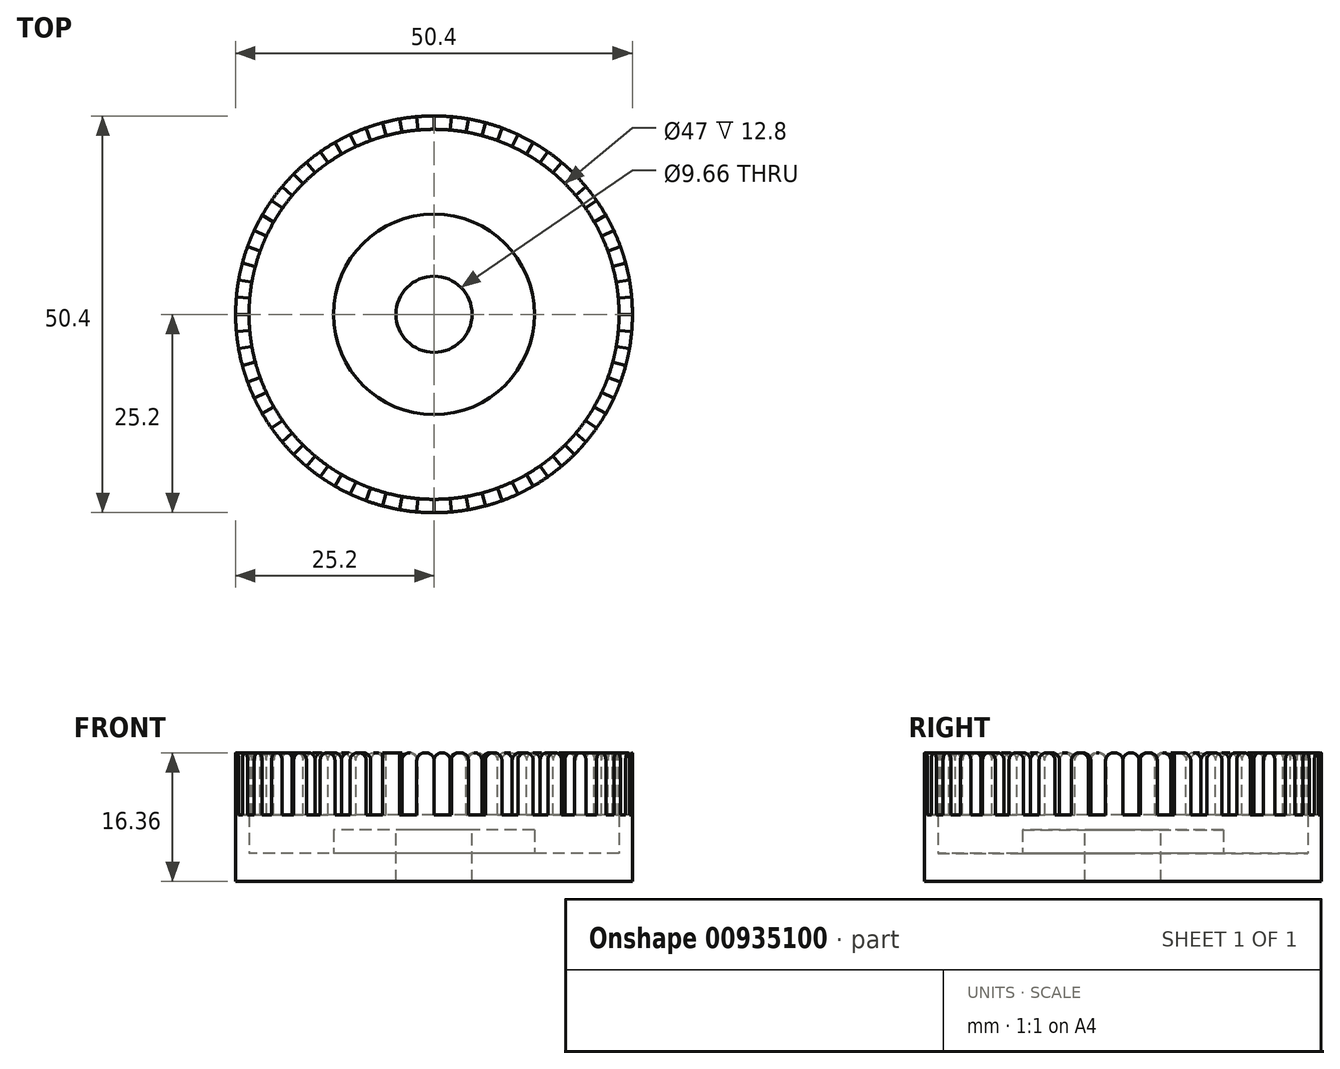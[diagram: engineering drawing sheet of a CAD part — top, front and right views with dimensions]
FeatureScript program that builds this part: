
annotation { "Feature Type Name" : "Feature", "Feature Type Description" : "" }
export const myFeature = defineFeature(function(context is Context, id is Id, definition is map)
    precondition{}
    {
        {
            var Q0;
            Q0=qCreatedBy(makeId("Top.planeOp"),FACE);
            var sketch = newSketch(context, id + "F0", { "sketchPlane" : qUnion([Q0])});
            skCircle(sketch, "E0", {"center": v(0, 0) * mm, "radius": 25.2 * mm});
            skSolve(sketch);
        }
        {
            var Q0;
            Q0 = qSketchRegion(id + "F0", true);
            var Q1;
            Q1=makeQuery(id+"F0.imprint","IMPRINT",FACE,{"disambiguationData":[TD([[makeQuery(id+"F0.imprint","IMPRINT",EDGE,{"derivedFrom":sQuery(id+"F0.wireOp",EDGE,"E0")}),1.0]])]});
            extrude(context, id + "F1", {"entities" : qUnion([Q0, Q1]), "depth" : 3.56 * mm, "offsetDistance" : 25 * mm});
        }
        {
            var Q0;
            Q0=makeQuery(id+"F1.opExtrude","CAP_FACE",FACE,{"disambiguationData":[OSD([sQuery(id+"F0.wireOp",EDGE,"E0")])],"isStart":false});
            var sketch = newSketch(context, id + "F2", { "sketchPlane" : qUnion([Q0])});
            skCircle(sketch, "E1", {"center": v(0, 0) * mm, "radius": 12.75 * mm});
            skSolve(sketch);
        }
        {
            var Q0;
            Q0 = qSketchRegion(id + "F2", true);
            var Q1;
            Q1=makeQuery(id+"F2.imprint","IMPRINT",FACE,{"disambiguationData":[TD([[makeQuery(id+"F2.imprint","IMPRINT",EDGE,{"derivedFrom":sQuery(id+"F2.wireOp",EDGE,"E1")}),1.0]])]});
            extrude(context, id + "F3", {"entities" : qUnion([Q0, Q1]), "operationType" : NewBodyOperationType.ADD, "depth" : 3 * mm, "offsetDistance" : 25 * mm});
        }
        {
            var Q0;
            Q0=makeQuery(id+"F1.opExtrude","CAP_FACE",FACE,{"disambiguationData":[OSD([sQuery(id+"F0.wireOp",EDGE,"E0")])],"isStart":false});
            var sketch = newSketch(context, id + "F4", { "sketchPlane" : qUnion([Q0])});
            skCircle(sketch, "E2", {"center": v(0, 0) * mm, "radius": 23.5 * mm});
            skSolve(sketch);
        }
        {
            var Q0;
            Q0=makeQuery(id+"F4.imprint","IMPRINT",FACE,{"disambiguationData":[TD([[makeQuery(id+"F4.imprint","IMPRINT",EDGE,{"derivedFrom":sQuery(id+"F4.wireOp",EDGE,"E2")}),-1.0]])]});
            extrude(context, id + "F5", {"entities" : qUnion([Q0]), "operationType" : NewBodyOperationType.ADD, "depth" : 12.8 * mm, "offsetDistance" : 25 * mm});
        }
        {
            var Q0;
            Q0=makeQuery(id+"F5.opExtrude","CAP_FACE",FACE,{"disambiguationData":[OSD([sQuery(id+"F0.wireOp",EDGE,"E0"),sQuery(id+"F4.wireOp",EDGE,"E2")])],"isStart":false});
            var sketch = newSketch(context, id + "F6", { "sketchPlane" : qUnion([Q0])});
            skLineSegment(sketch, "E3", {"start": v(0, -25.2) * mm, "end": v(0, 0) * mm, "construction": true});
            skLineSegment(sketch, "E4", {"start": v(0, -25.2) * mm, "end": v(0, -23.5) * mm});
            skLineSegment(sketch, "E5", {"start": v(2.2, -25.1) * mm, "end": v(2.05, -23.41) * mm});
            skLineSegment(sketch, "E6.1.0", {"start": v(4.38, -24.82) * mm, "end": v(4.08, -23.14) * mm});
            skLineSegment(sketch, "E6.2.0", {"start": v(6.52, -24.34) * mm, "end": v(6.08, -22.7) * mm});
            skLineSegment(sketch, "E6.3.0", {"start": v(8.62, -23.68) * mm, "end": v(8.04, -22.08) * mm});
            skLineSegment(sketch, "E6.4.0", {"start": v(10.65, -22.84) * mm, "end": v(9.93, -21.3) * mm});
            skLineSegment(sketch, "E6.5.0", {"start": v(12.6, -21.82) * mm, "end": v(11.75, -20.35) * mm});
            skLineSegment(sketch, "E6.6.0", {"start": v(14.45, -20.64) * mm, "end": v(13.48, -19.25) * mm});
            skLineSegment(sketch, "E6.7.0", {"start": v(16.2, -19.3) * mm, "end": v(15.1, -18) * mm});
            skLineSegment(sketch, "E6.8.0", {"start": v(17.82, -17.82) * mm, "end": v(16.62, -16.62) * mm});
            skLineSegment(sketch, "E6.9.0", {"start": v(19.3, -16.2) * mm, "end": v(18, -15.1) * mm});
            skLineSegment(sketch, "E6.10.0", {"start": v(20.64, -14.45) * mm, "end": v(19.25, -13.48) * mm});
            skLineSegment(sketch, "E6.11.0", {"start": v(21.82, -12.6) * mm, "end": v(20.35, -11.75) * mm});
            skLineSegment(sketch, "E6.12.0", {"start": v(22.84, -10.65) * mm, "end": v(21.3, -9.93) * mm});
            skLineSegment(sketch, "E6.13.0", {"start": v(23.68, -8.62) * mm, "end": v(22.08, -8.04) * mm});
            skLineSegment(sketch, "E6.14.0", {"start": v(24.34, -6.52) * mm, "end": v(22.7, -6.08) * mm});
            skLineSegment(sketch, "E6.15.0", {"start": v(24.82, -4.38) * mm, "end": v(23.14, -4.08) * mm});
            skLineSegment(sketch, "E6.16.0", {"start": v(25.1, -2.2) * mm, "end": v(23.41, -2.05) * mm});
            skLineSegment(sketch, "E6.17.0", {"start": v(25.2, 0) * mm, "end": v(23.5, 0) * mm});
            skLineSegment(sketch, "E6.18.0", {"start": v(25.1, 2.2) * mm, "end": v(23.41, 2.05) * mm});
            skLineSegment(sketch, "E6.19.0", {"start": v(24.82, 4.38) * mm, "end": v(23.14, 4.08) * mm});
            skLineSegment(sketch, "E6.20.0", {"start": v(24.34, 6.52) * mm, "end": v(22.7, 6.08) * mm});
            skLineSegment(sketch, "E6.21.0", {"start": v(23.68, 8.62) * mm, "end": v(22.08, 8.04) * mm});
            skLineSegment(sketch, "E6.22.0", {"start": v(22.84, 10.65) * mm, "end": v(21.3, 9.93) * mm});
            skLineSegment(sketch, "E6.23.0", {"start": v(21.82, 12.6) * mm, "end": v(20.35, 11.75) * mm});
            skLineSegment(sketch, "E6.24.0", {"start": v(20.64, 14.45) * mm, "end": v(19.25, 13.48) * mm});
            skLineSegment(sketch, "E6.25.0", {"start": v(19.3, 16.2) * mm, "end": v(18, 15.1) * mm});
            skLineSegment(sketch, "E6.26.0", {"start": v(17.82, 17.82) * mm, "end": v(16.62, 16.62) * mm});
            skLineSegment(sketch, "E6.27.0", {"start": v(16.2, 19.3) * mm, "end": v(15.1, 18) * mm});
            skLineSegment(sketch, "E6.28.0", {"start": v(14.45, 20.64) * mm, "end": v(13.48, 19.25) * mm});
            skLineSegment(sketch, "E6.29.0", {"start": v(12.6, 21.82) * mm, "end": v(11.75, 20.35) * mm});
            skLineSegment(sketch, "E6.30.0", {"start": v(10.65, 22.84) * mm, "end": v(9.93, 21.3) * mm});
            skLineSegment(sketch, "E6.31.0", {"start": v(8.62, 23.68) * mm, "end": v(8.04, 22.08) * mm});
            skLineSegment(sketch, "E6.32.0", {"start": v(6.52, 24.34) * mm, "end": v(6.08, 22.7) * mm});
            skLineSegment(sketch, "E6.33.0", {"start": v(4.38, 24.82) * mm, "end": v(4.08, 23.14) * mm});
            skLineSegment(sketch, "E6.34.0", {"start": v(2.2, 25.1) * mm, "end": v(2.05, 23.41) * mm});
            skLineSegment(sketch, "E6.35.0", {"start": v(0, 25.2) * mm, "end": v(0, 23.5) * mm});
            skLineSegment(sketch, "E6.36.0", {"start": v(-2.2, 25.1) * mm, "end": v(-2.05, 23.41) * mm});
            skLineSegment(sketch, "E6.37.0", {"start": v(-4.38, 24.82) * mm, "end": v(-4.08, 23.14) * mm});
            skLineSegment(sketch, "E6.38.0", {"start": v(-6.52, 24.34) * mm, "end": v(-6.08, 22.7) * mm});
            skLineSegment(sketch, "E6.39.0", {"start": v(-8.62, 23.68) * mm, "end": v(-8.04, 22.08) * mm});
            skLineSegment(sketch, "E6.40.0", {"start": v(-10.65, 22.84) * mm, "end": v(-9.93, 21.3) * mm});
            skLineSegment(sketch, "E6.41.0", {"start": v(-12.6, 21.82) * mm, "end": v(-11.75, 20.35) * mm});
            skLineSegment(sketch, "E6.42.0", {"start": v(-14.45, 20.64) * mm, "end": v(-13.48, 19.25) * mm});
            skLineSegment(sketch, "E6.43.0", {"start": v(-16.2, 19.3) * mm, "end": v(-15.1, 18) * mm});
            skLineSegment(sketch, "E6.44.0", {"start": v(-17.82, 17.82) * mm, "end": v(-16.62, 16.62) * mm});
            skLineSegment(sketch, "E6.45.0", {"start": v(-19.3, 16.2) * mm, "end": v(-18, 15.1) * mm});
            skLineSegment(sketch, "E6.46.0", {"start": v(-20.64, 14.45) * mm, "end": v(-19.25, 13.48) * mm});
            skLineSegment(sketch, "E6.47.0", {"start": v(-21.82, 12.6) * mm, "end": v(-20.35, 11.75) * mm});
            skLineSegment(sketch, "E6.48.0", {"start": v(-22.84, 10.65) * mm, "end": v(-21.3, 9.93) * mm});
            skLineSegment(sketch, "E6.49.0", {"start": v(-23.68, 8.62) * mm, "end": v(-22.08, 8.04) * mm});
            skLineSegment(sketch, "E6.50.0", {"start": v(-24.34, 6.52) * mm, "end": v(-22.7, 6.08) * mm});
            skLineSegment(sketch, "E6.51.0", {"start": v(-24.82, 4.38) * mm, "end": v(-23.14, 4.08) * mm});
            skLineSegment(sketch, "E6.52.0", {"start": v(-25.1, 2.2) * mm, "end": v(-23.41, 2.05) * mm});
            skLineSegment(sketch, "E6.53.0", {"start": v(-25.2, 0) * mm, "end": v(-23.5, 0) * mm});
            skLineSegment(sketch, "E6.54.0", {"start": v(-25.1, -2.2) * mm, "end": v(-23.41, -2.05) * mm});
            skLineSegment(sketch, "E6.55.0", {"start": v(-24.82, -4.38) * mm, "end": v(-23.14, -4.08) * mm});
            skLineSegment(sketch, "E6.56.0", {"start": v(-24.34, -6.52) * mm, "end": v(-22.7, -6.08) * mm});
            skLineSegment(sketch, "E6.57.0", {"start": v(-23.68, -8.62) * mm, "end": v(-22.08, -8.04) * mm});
            skLineSegment(sketch, "E6.58.0", {"start": v(-22.84, -10.65) * mm, "end": v(-21.3, -9.93) * mm});
            skLineSegment(sketch, "E6.59.0", {"start": v(-21.82, -12.6) * mm, "end": v(-20.35, -11.75) * mm});
            skLineSegment(sketch, "E6.60.0", {"start": v(-20.64, -14.45) * mm, "end": v(-19.25, -13.48) * mm});
            skLineSegment(sketch, "E6.61.0", {"start": v(-19.3, -16.2) * mm, "end": v(-18, -15.1) * mm});
            skLineSegment(sketch, "E6.62.0", {"start": v(-17.82, -17.82) * mm, "end": v(-16.62, -16.62) * mm});
            skLineSegment(sketch, "E6.63.0", {"start": v(-16.2, -19.3) * mm, "end": v(-15.1, -18) * mm});
            skLineSegment(sketch, "E6.64.0", {"start": v(-14.45, -20.64) * mm, "end": v(-13.48, -19.25) * mm});
            skLineSegment(sketch, "E6.65.0", {"start": v(-12.6, -21.82) * mm, "end": v(-11.75, -20.35) * mm});
            skLineSegment(sketch, "E6.66.0", {"start": v(-10.65, -22.84) * mm, "end": v(-9.93, -21.3) * mm});
            skLineSegment(sketch, "E6.67.0", {"start": v(-8.62, -23.68) * mm, "end": v(-8.04, -22.08) * mm});
            skLineSegment(sketch, "E6.68.0", {"start": v(-6.52, -24.34) * mm, "end": v(-6.08, -22.7) * mm});
            skLineSegment(sketch, "E6.69.0", {"start": v(-4.38, -24.82) * mm, "end": v(-4.08, -23.14) * mm});
            skLineSegment(sketch, "E6.70.0", {"start": v(-2.2, -25.1) * mm, "end": v(-2.05, -23.41) * mm});
            skPoint(sketch, "E6.center", {"position": v(0, 0) * mm});
            skSolve(sketch);
        }
        {
            var Q0;
            {var subQ0=sQuery(id+"F6.wireOp",EDGE,"E5");Q0=makeQuery(id+"F6.imprint","IMPRINT",FACE,{"disambiguationData":[TD([[makeQuery(id+"F6.imprint","IMPRINT",EDGE,{"derivedFrom":subQ0}),1.0]])]});}
            var Q1;
            {var subQ0=sQuery(id+"F6.wireOp",EDGE,"E6.1.0");Q1=makeQuery(id+"F6.imprint","IMPRINT",FACE,{"disambiguationData":[TD([[makeQuery(id+"F6.imprint","IMPRINT",EDGE,{"derivedFrom":subQ0}),-1.0]])]});}
            var Q2;
            {var subQ0=sQuery(id+"F6.wireOp",EDGE,"E6.3.0");Q2=makeQuery(id+"F6.imprint","IMPRINT",FACE,{"disambiguationData":[TD([[makeQuery(id+"F6.imprint","IMPRINT",EDGE,{"derivedFrom":subQ0}),-1.0]])]});}
            var Q3;
            {var subQ0=sQuery(id+"F6.wireOp",EDGE,"E6.5.0");Q3=makeQuery(id+"F6.imprint","IMPRINT",FACE,{"disambiguationData":[TD([[makeQuery(id+"F6.imprint","IMPRINT",EDGE,{"derivedFrom":subQ0}),-1.0]])]});}
            var Q4;
            {var subQ0=sQuery(id+"F6.wireOp",EDGE,"E6.7.0");Q4=makeQuery(id+"F6.imprint","IMPRINT",FACE,{"disambiguationData":[TD([[makeQuery(id+"F6.imprint","IMPRINT",EDGE,{"derivedFrom":subQ0}),-1.0]])]});}
            var Q5;
            {var subQ0=sQuery(id+"F6.wireOp",EDGE,"E6.9.0");Q5=makeQuery(id+"F6.imprint","IMPRINT",FACE,{"disambiguationData":[TD([[makeQuery(id+"F6.imprint","IMPRINT",EDGE,{"derivedFrom":subQ0}),-1.0]])]});}
            var Q6;
            {var subQ0=sQuery(id+"F6.wireOp",EDGE,"E6.11.0");Q6=makeQuery(id+"F6.imprint","IMPRINT",FACE,{"disambiguationData":[TD([[makeQuery(id+"F6.imprint","IMPRINT",EDGE,{"derivedFrom":subQ0}),-1.0]])]});}
            var Q7;
            {var subQ0=sQuery(id+"F6.wireOp",EDGE,"E6.13.0");Q7=makeQuery(id+"F6.imprint","IMPRINT",FACE,{"disambiguationData":[TD([[makeQuery(id+"F6.imprint","IMPRINT",EDGE,{"derivedFrom":subQ0}),-1.0]])]});}
            var Q8;
            {var subQ0=sQuery(id+"F6.wireOp",EDGE,"E6.15.0");Q8=makeQuery(id+"F6.imprint","IMPRINT",FACE,{"disambiguationData":[TD([[makeQuery(id+"F6.imprint","IMPRINT",EDGE,{"derivedFrom":subQ0}),-1.0]])]});}
            var Q9;
            {var subQ0=sQuery(id+"F6.wireOp",EDGE,"E6.17.0");Q9=makeQuery(id+"F6.imprint","IMPRINT",FACE,{"disambiguationData":[TD([[makeQuery(id+"F6.imprint","IMPRINT",EDGE,{"derivedFrom":subQ0}),-1.0]])]});}
            var Q10;
            {var subQ0=sQuery(id+"F6.wireOp",EDGE,"E6.19.0");Q10=makeQuery(id+"F6.imprint","IMPRINT",FACE,{"disambiguationData":[TD([[makeQuery(id+"F6.imprint","IMPRINT",EDGE,{"derivedFrom":subQ0}),-1.0]])]});}
            var Q11;
            {var subQ0=sQuery(id+"F6.wireOp",EDGE,"E6.21.0");Q11=makeQuery(id+"F6.imprint","IMPRINT",FACE,{"disambiguationData":[TD([[makeQuery(id+"F6.imprint","IMPRINT",EDGE,{"derivedFrom":subQ0}),-1.0]])]});}
            var Q12;
            {var subQ0=sQuery(id+"F6.wireOp",EDGE,"E6.23.0");Q12=makeQuery(id+"F6.imprint","IMPRINT",FACE,{"disambiguationData":[TD([[makeQuery(id+"F6.imprint","IMPRINT",EDGE,{"derivedFrom":subQ0}),-1.0]])]});}
            var Q13;
            {var subQ0=sQuery(id+"F6.wireOp",EDGE,"E6.25.0");Q13=makeQuery(id+"F6.imprint","IMPRINT",FACE,{"disambiguationData":[TD([[makeQuery(id+"F6.imprint","IMPRINT",EDGE,{"derivedFrom":subQ0}),-1.0]])]});}
            var Q14;
            {var subQ0=sQuery(id+"F6.wireOp",EDGE,"E6.27.0");Q14=makeQuery(id+"F6.imprint","IMPRINT",FACE,{"disambiguationData":[TD([[makeQuery(id+"F6.imprint","IMPRINT",EDGE,{"derivedFrom":subQ0}),-1.0]])]});}
            var Q15;
            {var subQ0=sQuery(id+"F6.wireOp",EDGE,"E6.29.0");Q15=makeQuery(id+"F6.imprint","IMPRINT",FACE,{"disambiguationData":[TD([[makeQuery(id+"F6.imprint","IMPRINT",EDGE,{"derivedFrom":subQ0}),-1.0]])]});}
            var Q16;
            {var subQ0=sQuery(id+"F6.wireOp",EDGE,"E6.31.0");Q16=makeQuery(id+"F6.imprint","IMPRINT",FACE,{"disambiguationData":[TD([[makeQuery(id+"F6.imprint","IMPRINT",EDGE,{"derivedFrom":subQ0}),-1.0]])]});}
            var Q17;
            {var subQ0=sQuery(id+"F6.wireOp",EDGE,"E6.33.0");Q17=makeQuery(id+"F6.imprint","IMPRINT",FACE,{"disambiguationData":[TD([[makeQuery(id+"F6.imprint","IMPRINT",EDGE,{"derivedFrom":subQ0}),-1.0]])]});}
            var Q18;
            {var subQ0=sQuery(id+"F6.wireOp",EDGE,"E6.35.0");Q18=makeQuery(id+"F6.imprint","IMPRINT",FACE,{"disambiguationData":[TD([[makeQuery(id+"F6.imprint","IMPRINT",EDGE,{"derivedFrom":subQ0}),-1.0]])]});}
            var Q19;
            {var subQ0=sQuery(id+"F6.wireOp",EDGE,"E6.37.0");Q19=makeQuery(id+"F6.imprint","IMPRINT",FACE,{"disambiguationData":[TD([[makeQuery(id+"F6.imprint","IMPRINT",EDGE,{"derivedFrom":subQ0}),-1.0]])]});}
            var Q20;
            {var subQ0=sQuery(id+"F6.wireOp",EDGE,"E6.39.0");Q20=makeQuery(id+"F6.imprint","IMPRINT",FACE,{"disambiguationData":[TD([[makeQuery(id+"F6.imprint","IMPRINT",EDGE,{"derivedFrom":subQ0}),-1.0]])]});}
            var Q21;
            {var subQ0=sQuery(id+"F6.wireOp",EDGE,"E6.41.0");Q21=makeQuery(id+"F6.imprint","IMPRINT",FACE,{"disambiguationData":[TD([[makeQuery(id+"F6.imprint","IMPRINT",EDGE,{"derivedFrom":subQ0}),-1.0]])]});}
            var Q22;
            {var subQ0=sQuery(id+"F6.wireOp",EDGE,"E6.43.0");Q22=makeQuery(id+"F6.imprint","IMPRINT",FACE,{"disambiguationData":[TD([[makeQuery(id+"F6.imprint","IMPRINT",EDGE,{"derivedFrom":subQ0}),-1.0]])]});}
            var Q23;
            {var subQ0=sQuery(id+"F6.wireOp",EDGE,"E6.45.0");Q23=makeQuery(id+"F6.imprint","IMPRINT",FACE,{"disambiguationData":[TD([[makeQuery(id+"F6.imprint","IMPRINT",EDGE,{"derivedFrom":subQ0}),-1.0]])]});}
            var Q24;
            {var subQ0=sQuery(id+"F6.wireOp",EDGE,"E6.47.0");Q24=makeQuery(id+"F6.imprint","IMPRINT",FACE,{"disambiguationData":[TD([[makeQuery(id+"F6.imprint","IMPRINT",EDGE,{"derivedFrom":subQ0}),-1.0]])]});}
            var Q25;
            {var subQ0=makeQuery(id+"F5.opExtrude","CAP_EDGE",EDGE,{"disambiguationData":[OSD([sQuery(id+"F4.wireOp",EDGE,"E2")])],"isStart":false});var subQ33=makeQuery(id+"F6.imprint","INTERSECT",VERTEX,{"derivedFrom":[subQ0,sQuery(id+"F6.wireOp",EDGE,"E5")]});Q25=makeQuery(id+"F6.imprint","IMPRINT",FACE,{"disambiguationData":[TD([[makeQuery(id+"F6.imprint","IMPRINT",EDGE,{"disambiguationData":[TD([[subQ33,-1.0]])],"derivedFrom":subQ0}),1.0]])]});}
            var Q26;
            {var subQ0=sQuery(id+"F6.wireOp",EDGE,"E6.49.0");Q26=makeQuery(id+"F6.imprint","IMPRINT",FACE,{"disambiguationData":[TD([[makeQuery(id+"F6.imprint","IMPRINT",EDGE,{"derivedFrom":subQ0}),-1.0]])]});}
            var Q27;
            {var subQ0=sQuery(id+"F6.wireOp",EDGE,"E6.51.0");Q27=makeQuery(id+"F6.imprint","IMPRINT",FACE,{"disambiguationData":[TD([[makeQuery(id+"F6.imprint","IMPRINT",EDGE,{"derivedFrom":subQ0}),-1.0]])]});}
            var Q28;
            {var subQ0=sQuery(id+"F6.wireOp",EDGE,"E6.53.0");Q28=makeQuery(id+"F6.imprint","IMPRINT",FACE,{"disambiguationData":[TD([[makeQuery(id+"F6.imprint","IMPRINT",EDGE,{"derivedFrom":subQ0}),-1.0]])]});}
            var Q29;
            {var subQ0=sQuery(id+"F6.wireOp",EDGE,"E6.55.0");Q29=makeQuery(id+"F6.imprint","IMPRINT",FACE,{"disambiguationData":[TD([[makeQuery(id+"F6.imprint","IMPRINT",EDGE,{"derivedFrom":subQ0}),-1.0]])]});}
            var Q30;
            {var subQ0=sQuery(id+"F6.wireOp",EDGE,"E6.57.0");Q30=makeQuery(id+"F6.imprint","IMPRINT",FACE,{"disambiguationData":[TD([[makeQuery(id+"F6.imprint","IMPRINT",EDGE,{"derivedFrom":subQ0}),-1.0]])]});}
            var Q31;
            {var subQ0=sQuery(id+"F6.wireOp",EDGE,"E6.59.0");Q31=makeQuery(id+"F6.imprint","IMPRINT",FACE,{"disambiguationData":[TD([[makeQuery(id+"F6.imprint","IMPRINT",EDGE,{"derivedFrom":subQ0}),-1.0]])]});}
            var Q32;
            {var subQ0=sQuery(id+"F6.wireOp",EDGE,"E6.61.0");Q32=makeQuery(id+"F6.imprint","IMPRINT",FACE,{"disambiguationData":[TD([[makeQuery(id+"F6.imprint","IMPRINT",EDGE,{"derivedFrom":subQ0}),-1.0]])]});}
            var Q33;
            {var subQ0=sQuery(id+"F6.wireOp",EDGE,"E6.63.0");Q33=makeQuery(id+"F6.imprint","IMPRINT",FACE,{"disambiguationData":[TD([[makeQuery(id+"F6.imprint","IMPRINT",EDGE,{"derivedFrom":subQ0}),-1.0]])]});}
            var Q34;
            {var subQ0=sQuery(id+"F6.wireOp",EDGE,"E6.65.0");Q34=makeQuery(id+"F6.imprint","IMPRINT",FACE,{"disambiguationData":[TD([[makeQuery(id+"F6.imprint","IMPRINT",EDGE,{"derivedFrom":subQ0}),-1.0]])]});}
            var Q35;
            {var subQ0=sQuery(id+"F6.wireOp",EDGE,"E6.67.0");Q35=makeQuery(id+"F6.imprint","IMPRINT",FACE,{"disambiguationData":[TD([[makeQuery(id+"F6.imprint","IMPRINT",EDGE,{"derivedFrom":subQ0}),-1.0]])]});}
            var Q36;
            {var subQ0=sQuery(id+"F6.wireOp",EDGE,"E6.69.0");Q36=makeQuery(id+"F6.imprint","IMPRINT",FACE,{"disambiguationData":[TD([[makeQuery(id+"F6.imprint","IMPRINT",EDGE,{"derivedFrom":subQ0}),-1.0]])]});}
            extrude(context, id + "F7", {"entities" : qUnion([Q0, Q1, Q2, Q3, Q4, Q5, Q6, Q7, Q8, Q9, Q10, Q11, Q12, Q13, Q14, Q15, Q16, Q17, Q18, Q19, Q20, Q21, Q22, Q23, Q24, Q25, Q26, Q27, Q28, Q29, Q30, Q31, Q32, Q33, Q34, Q35, Q36]), "operationType" : NewBodyOperationType.REMOVE, "oppositeDirection" : true, "depth" : 7.9 * mm, "offsetDistance" : 25 * mm});
        }
        {
            var Q0;
            Q0=makeQuery(id+"F7.boolean.opBoolean","COPY",EDGE,{"derivedFrom":makeQuery(id+"F7.opExtrude","CAP_EDGE",EDGE,{"disambiguationData":[OSD([sQuery(id+"F6.wireOp",EDGE,"E6.2.0")])],"isStart":true})});
            var Q1;
            Q1=makeQuery(id+"F7.boolean.opBoolean","COPY",EDGE,{"derivedFrom":makeQuery(id+"F7.opExtrude","CAP_EDGE",EDGE,{"disambiguationData":[OSD([sQuery(id+"F6.wireOp",EDGE,"E6.3.0")])],"isStart":true})});
            var Q2;
            Q2=makeQuery(id+"F7.boolean.opBoolean","COPY",EDGE,{"derivedFrom":makeQuery(id+"F7.opExtrude","CAP_EDGE",EDGE,{"disambiguationData":[OSD([sQuery(id+"F6.wireOp",EDGE,"E6.4.0")])],"isStart":true})});
            var Q3;
            Q3=makeQuery(id+"F7.boolean.opBoolean","COPY",EDGE,{"derivedFrom":makeQuery(id+"F7.opExtrude","CAP_EDGE",EDGE,{"disambiguationData":[OSD([sQuery(id+"F6.wireOp",EDGE,"E6.5.0")])],"isStart":true})});
            var Q4;
            Q4=makeQuery(id+"F7.boolean.opBoolean","COPY",EDGE,{"derivedFrom":makeQuery(id+"F7.opExtrude","CAP_EDGE",EDGE,{"disambiguationData":[OSD([sQuery(id+"F6.wireOp",EDGE,"E6.6.0")])],"isStart":true})});
            var Q5;
            Q5=makeQuery(id+"F7.boolean.opBoolean","COPY",EDGE,{"derivedFrom":makeQuery(id+"F7.opExtrude","CAP_EDGE",EDGE,{"disambiguationData":[OSD([sQuery(id+"F6.wireOp",EDGE,"E6.7.0")])],"isStart":true})});
            var Q6;
            Q6=makeQuery(id+"F7.boolean.opBoolean","COPY",EDGE,{"derivedFrom":makeQuery(id+"F7.opExtrude","CAP_EDGE",EDGE,{"disambiguationData":[OSD([sQuery(id+"F6.wireOp",EDGE,"E6.8.0")])],"isStart":true})});
            var Q7;
            Q7=makeQuery(id+"F7.boolean.opBoolean","COPY",EDGE,{"derivedFrom":makeQuery(id+"F7.opExtrude","CAP_EDGE",EDGE,{"disambiguationData":[OSD([sQuery(id+"F6.wireOp",EDGE,"E6.9.0")])],"isStart":true})});
            var Q8;
            Q8=makeQuery(id+"F7.boolean.opBoolean","COPY",EDGE,{"derivedFrom":makeQuery(id+"F7.opExtrude","CAP_EDGE",EDGE,{"disambiguationData":[OSD([sQuery(id+"F6.wireOp",EDGE,"E6.10.0")])],"isStart":true})});
            var Q9;
            Q9=makeQuery(id+"F7.boolean.opBoolean","COPY",EDGE,{"derivedFrom":makeQuery(id+"F7.opExtrude","CAP_EDGE",EDGE,{"disambiguationData":[OSD([sQuery(id+"F6.wireOp",EDGE,"E6.11.0")])],"isStart":true})});
            var Q10;
            Q10=makeQuery(id+"F7.boolean.opBoolean","COPY",EDGE,{"derivedFrom":makeQuery(id+"F7.opExtrude","CAP_EDGE",EDGE,{"disambiguationData":[OSD([sQuery(id+"F6.wireOp",EDGE,"E6.12.0")])],"isStart":true})});
            var Q11;
            Q11=makeQuery(id+"F7.boolean.opBoolean","COPY",EDGE,{"derivedFrom":makeQuery(id+"F7.opExtrude","CAP_EDGE",EDGE,{"disambiguationData":[OSD([sQuery(id+"F6.wireOp",EDGE,"E6.13.0")])],"isStart":true})});
            var Q12;
            Q12=makeQuery(id+"F7.boolean.opBoolean","COPY",EDGE,{"derivedFrom":makeQuery(id+"F7.opExtrude","CAP_EDGE",EDGE,{"disambiguationData":[OSD([sQuery(id+"F6.wireOp",EDGE,"E6.14.0")])],"isStart":true})});
            var Q13;
            Q13=makeQuery(id+"F7.boolean.opBoolean","COPY",EDGE,{"derivedFrom":makeQuery(id+"F7.opExtrude","CAP_EDGE",EDGE,{"disambiguationData":[OSD([sQuery(id+"F6.wireOp",EDGE,"E6.15.0")])],"isStart":true})});
            var Q14;
            Q14=makeQuery(id+"F7.boolean.opBoolean","COPY",EDGE,{"derivedFrom":makeQuery(id+"F7.opExtrude","CAP_EDGE",EDGE,{"disambiguationData":[OSD([sQuery(id+"F6.wireOp",EDGE,"E6.16.0")])],"isStart":true})});
            var Q15;
            Q15=makeQuery(id+"F7.boolean.opBoolean","COPY",EDGE,{"derivedFrom":makeQuery(id+"F7.opExtrude","CAP_EDGE",EDGE,{"disambiguationData":[OSD([sQuery(id+"F6.wireOp",EDGE,"E6.17.0")])],"isStart":true})});
            var Q16;
            Q16=makeQuery(id+"F7.boolean.opBoolean","COPY",EDGE,{"derivedFrom":makeQuery(id+"F7.opExtrude","CAP_EDGE",EDGE,{"disambiguationData":[OSD([sQuery(id+"F6.wireOp",EDGE,"E6.18.0")])],"isStart":true})});
            var Q17;
            Q17=makeQuery(id+"F7.boolean.opBoolean","COPY",EDGE,{"derivedFrom":makeQuery(id+"F7.opExtrude","CAP_EDGE",EDGE,{"disambiguationData":[OSD([sQuery(id+"F6.wireOp",EDGE,"E6.19.0")])],"isStart":true})});
            var Q18;
            Q18=makeQuery(id+"F7.boolean.opBoolean","COPY",EDGE,{"derivedFrom":makeQuery(id+"F7.opExtrude","CAP_EDGE",EDGE,{"disambiguationData":[OSD([sQuery(id+"F6.wireOp",EDGE,"E6.21.0")])],"isStart":true})});
            var Q19;
            Q19=makeQuery(id+"F7.boolean.opBoolean","COPY",EDGE,{"derivedFrom":makeQuery(id+"F7.opExtrude","CAP_EDGE",EDGE,{"disambiguationData":[OSD([sQuery(id+"F6.wireOp",EDGE,"E6.22.0")])],"isStart":true})});
            var Q20;
            Q20=makeQuery(id+"F7.boolean.opBoolean","COPY",EDGE,{"derivedFrom":makeQuery(id+"F7.opExtrude","CAP_EDGE",EDGE,{"disambiguationData":[OSD([sQuery(id+"F6.wireOp",EDGE,"E6.23.0")])],"isStart":true})});
            var Q21;
            Q21=makeQuery(id+"F7.boolean.opBoolean","COPY",EDGE,{"derivedFrom":makeQuery(id+"F7.opExtrude","CAP_EDGE",EDGE,{"disambiguationData":[OSD([sQuery(id+"F6.wireOp",EDGE,"E6.24.0")])],"isStart":true})});
            var Q22;
            Q22=makeQuery(id+"F7.boolean.opBoolean","COPY",EDGE,{"derivedFrom":makeQuery(id+"F7.opExtrude","CAP_EDGE",EDGE,{"disambiguationData":[OSD([sQuery(id+"F6.wireOp",EDGE,"E6.25.0")])],"isStart":true})});
            var Q23;
            Q23=makeQuery(id+"F7.boolean.opBoolean","COPY",EDGE,{"derivedFrom":makeQuery(id+"F7.opExtrude","CAP_EDGE",EDGE,{"disambiguationData":[OSD([sQuery(id+"F6.wireOp",EDGE,"E6.26.0")])],"isStart":true})});
            var Q24;
            Q24=makeQuery(id+"F7.boolean.opBoolean","COPY",EDGE,{"derivedFrom":makeQuery(id+"F7.opExtrude","CAP_EDGE",EDGE,{"disambiguationData":[OSD([sQuery(id+"F6.wireOp",EDGE,"E6.27.0")])],"isStart":true})});
            var Q25;
            Q25=makeQuery(id+"F7.boolean.opBoolean","COPY",EDGE,{"derivedFrom":makeQuery(id+"F7.opExtrude","CAP_EDGE",EDGE,{"disambiguationData":[OSD([sQuery(id+"F6.wireOp",EDGE,"E6.28.0")])],"isStart":true})});
            var Q26;
            Q26=makeQuery(id+"F7.boolean.opBoolean","COPY",EDGE,{"derivedFrom":makeQuery(id+"F7.opExtrude","CAP_EDGE",EDGE,{"disambiguationData":[OSD([sQuery(id+"F6.wireOp",EDGE,"E6.29.0")])],"isStart":true})});
            var Q27;
            Q27=makeQuery(id+"F7.boolean.opBoolean","COPY",EDGE,{"derivedFrom":makeQuery(id+"F7.opExtrude","CAP_EDGE",EDGE,{"disambiguationData":[OSD([sQuery(id+"F6.wireOp",EDGE,"E6.30.0")])],"isStart":true})});
            var Q28;
            Q28=makeQuery(id+"F7.boolean.opBoolean","COPY",EDGE,{"derivedFrom":makeQuery(id+"F7.opExtrude","CAP_EDGE",EDGE,{"disambiguationData":[OSD([sQuery(id+"F6.wireOp",EDGE,"E6.31.0")])],"isStart":true})});
            var Q29;
            Q29=makeQuery(id+"F7.boolean.opBoolean","COPY",EDGE,{"derivedFrom":makeQuery(id+"F7.opExtrude","CAP_EDGE",EDGE,{"disambiguationData":[OSD([sQuery(id+"F6.wireOp",EDGE,"E6.32.0")])],"isStart":true})});
            var Q30;
            Q30=makeQuery(id+"F7.boolean.opBoolean","COPY",EDGE,{"derivedFrom":makeQuery(id+"F7.opExtrude","CAP_EDGE",EDGE,{"disambiguationData":[OSD([sQuery(id+"F6.wireOp",EDGE,"E6.33.0")])],"isStart":true})});
            var Q31;
            Q31=makeQuery(id+"F7.boolean.opBoolean","COPY",EDGE,{"derivedFrom":makeQuery(id+"F7.opExtrude","CAP_EDGE",EDGE,{"disambiguationData":[OSD([sQuery(id+"F6.wireOp",EDGE,"E6.34.0")])],"isStart":true})});
            var Q32;
            Q32=makeQuery(id+"F7.boolean.opBoolean","COPY",EDGE,{"derivedFrom":makeQuery(id+"F7.opExtrude","CAP_EDGE",EDGE,{"disambiguationData":[OSD([sQuery(id+"F6.wireOp",EDGE,"E6.35.0")])],"isStart":true})});
            var Q33;
            Q33=makeQuery(id+"F7.boolean.opBoolean","COPY",EDGE,{"derivedFrom":makeQuery(id+"F7.opExtrude","CAP_EDGE",EDGE,{"disambiguationData":[OSD([sQuery(id+"F6.wireOp",EDGE,"E6.36.0")])],"isStart":true})});
            var Q34;
            Q34=makeQuery(id+"F7.boolean.opBoolean","COPY",EDGE,{"derivedFrom":makeQuery(id+"F7.opExtrude","CAP_EDGE",EDGE,{"disambiguationData":[OSD([sQuery(id+"F6.wireOp",EDGE,"E6.37.0")])],"isStart":true})});
            var Q35;
            Q35=makeQuery(id+"F7.boolean.opBoolean","COPY",EDGE,{"derivedFrom":makeQuery(id+"F7.opExtrude","CAP_EDGE",EDGE,{"disambiguationData":[OSD([sQuery(id+"F6.wireOp",EDGE,"E6.38.0")])],"isStart":true})});
            var Q36;
            Q36=makeQuery(id+"F7.boolean.opBoolean","COPY",EDGE,{"derivedFrom":makeQuery(id+"F7.opExtrude","CAP_EDGE",EDGE,{"disambiguationData":[OSD([sQuery(id+"F6.wireOp",EDGE,"E6.39.0")])],"isStart":true})});
            var Q37;
            Q37=makeQuery(id+"F7.boolean.opBoolean","COPY",EDGE,{"derivedFrom":makeQuery(id+"F7.opExtrude","CAP_EDGE",EDGE,{"disambiguationData":[OSD([sQuery(id+"F6.wireOp",EDGE,"E6.40.0")])],"isStart":true})});
            var Q38;
            Q38=makeQuery(id+"F7.boolean.opBoolean","COPY",EDGE,{"derivedFrom":makeQuery(id+"F7.opExtrude","CAP_EDGE",EDGE,{"disambiguationData":[OSD([sQuery(id+"F6.wireOp",EDGE,"E6.41.0")])],"isStart":true})});
            var Q39;
            Q39=makeQuery(id+"F7.boolean.opBoolean","COPY",EDGE,{"derivedFrom":makeQuery(id+"F7.opExtrude","CAP_EDGE",EDGE,{"disambiguationData":[OSD([sQuery(id+"F6.wireOp",EDGE,"E6.42.0")])],"isStart":true})});
            var Q40;
            Q40=makeQuery(id+"F7.boolean.opBoolean","COPY",EDGE,{"derivedFrom":makeQuery(id+"F7.opExtrude","CAP_EDGE",EDGE,{"disambiguationData":[OSD([sQuery(id+"F6.wireOp",EDGE,"E6.43.0")])],"isStart":true})});
            var Q41;
            Q41=makeQuery(id+"F7.boolean.opBoolean","COPY",EDGE,{"derivedFrom":makeQuery(id+"F7.opExtrude","CAP_EDGE",EDGE,{"disambiguationData":[OSD([sQuery(id+"F6.wireOp",EDGE,"E6.44.0")])],"isStart":true})});
            var Q42;
            Q42=makeQuery(id+"F7.boolean.opBoolean","COPY",EDGE,{"derivedFrom":makeQuery(id+"F7.opExtrude","CAP_EDGE",EDGE,{"disambiguationData":[OSD([sQuery(id+"F6.wireOp",EDGE,"E6.45.0")])],"isStart":true})});
            var Q43;
            Q43=makeQuery(id+"F7.boolean.opBoolean","COPY",EDGE,{"derivedFrom":makeQuery(id+"F7.opExtrude","CAP_EDGE",EDGE,{"disambiguationData":[OSD([sQuery(id+"F6.wireOp",EDGE,"E6.47.0")])],"isStart":true})});
            var Q44;
            Q44=makeQuery(id+"F7.boolean.opBoolean","COPY",EDGE,{"derivedFrom":makeQuery(id+"F7.opExtrude","CAP_EDGE",EDGE,{"disambiguationData":[OSD([sQuery(id+"F6.wireOp",EDGE,"E6.46.0")])],"isStart":true})});
            var Q45;
            Q45=makeQuery(id+"F7.boolean.opBoolean","COPY",EDGE,{"derivedFrom":makeQuery(id+"F7.opExtrude","CAP_EDGE",EDGE,{"disambiguationData":[OSD([sQuery(id+"F6.wireOp",EDGE,"E6.48.0")])],"isStart":true})});
            var Q46;
            Q46=makeQuery(id+"F7.boolean.opBoolean","COPY",EDGE,{"derivedFrom":makeQuery(id+"F7.opExtrude","CAP_EDGE",EDGE,{"disambiguationData":[OSD([sQuery(id+"F6.wireOp",EDGE,"E6.49.0")])],"isStart":true})});
            var Q47;
            Q47=makeQuery(id+"F7.boolean.opBoolean","COPY",EDGE,{"derivedFrom":makeQuery(id+"F7.opExtrude","CAP_EDGE",EDGE,{"disambiguationData":[OSD([sQuery(id+"F6.wireOp",EDGE,"E6.50.0")])],"isStart":true})});
            var Q48;
            Q48=makeQuery(id+"F7.boolean.opBoolean","COPY",EDGE,{"derivedFrom":makeQuery(id+"F7.opExtrude","CAP_EDGE",EDGE,{"disambiguationData":[OSD([sQuery(id+"F6.wireOp",EDGE,"E6.51.0")])],"isStart":true})});
            var Q49;
            Q49=makeQuery(id+"F7.boolean.opBoolean","COPY",EDGE,{"derivedFrom":makeQuery(id+"F7.opExtrude","CAP_EDGE",EDGE,{"disambiguationData":[OSD([sQuery(id+"F6.wireOp",EDGE,"E6.52.0")])],"isStart":true})});
            var Q50;
            Q50=makeQuery(id+"F7.boolean.opBoolean","COPY",EDGE,{"derivedFrom":makeQuery(id+"F7.opExtrude","CAP_EDGE",EDGE,{"disambiguationData":[OSD([sQuery(id+"F6.wireOp",EDGE,"E6.53.0")])],"isStart":true})});
            var Q51;
            Q51=makeQuery(id+"F7.boolean.opBoolean","COPY",EDGE,{"derivedFrom":makeQuery(id+"F7.opExtrude","CAP_EDGE",EDGE,{"disambiguationData":[OSD([sQuery(id+"F6.wireOp",EDGE,"E6.54.0")])],"isStart":true})});
            var Q52;
            Q52=makeQuery(id+"F7.boolean.opBoolean","COPY",EDGE,{"derivedFrom":makeQuery(id+"F7.opExtrude","CAP_EDGE",EDGE,{"disambiguationData":[OSD([sQuery(id+"F6.wireOp",EDGE,"E6.55.0")])],"isStart":true})});
            var Q53;
            Q53=makeQuery(id+"F7.boolean.opBoolean","COPY",EDGE,{"derivedFrom":makeQuery(id+"F7.opExtrude","CAP_EDGE",EDGE,{"disambiguationData":[OSD([sQuery(id+"F6.wireOp",EDGE,"E6.56.0")])],"isStart":true})});
            var Q54;
            Q54=makeQuery(id+"F7.boolean.opBoolean","COPY",EDGE,{"derivedFrom":makeQuery(id+"F7.opExtrude","CAP_EDGE",EDGE,{"disambiguationData":[OSD([sQuery(id+"F6.wireOp",EDGE,"E6.57.0")])],"isStart":true})});
            var Q55;
            Q55=makeQuery(id+"F7.boolean.opBoolean","COPY",EDGE,{"derivedFrom":makeQuery(id+"F7.opExtrude","CAP_EDGE",EDGE,{"disambiguationData":[OSD([sQuery(id+"F6.wireOp",EDGE,"E6.58.0")])],"isStart":true})});
            var Q56;
            Q56=makeQuery(id+"F7.boolean.opBoolean","COPY",EDGE,{"derivedFrom":makeQuery(id+"F7.opExtrude","CAP_EDGE",EDGE,{"disambiguationData":[OSD([sQuery(id+"F6.wireOp",EDGE,"E6.59.0")])],"isStart":true})});
            var Q57;
            Q57=makeQuery(id+"F7.boolean.opBoolean","COPY",EDGE,{"derivedFrom":makeQuery(id+"F7.opExtrude","CAP_EDGE",EDGE,{"disambiguationData":[OSD([sQuery(id+"F6.wireOp",EDGE,"E6.60.0")])],"isStart":true})});
            var Q58;
            Q58=makeQuery(id+"F7.boolean.opBoolean","COPY",EDGE,{"derivedFrom":makeQuery(id+"F7.opExtrude","CAP_EDGE",EDGE,{"disambiguationData":[OSD([sQuery(id+"F6.wireOp",EDGE,"E6.61.0")])],"isStart":true})});
            var Q59;
            Q59=makeQuery(id+"F7.boolean.opBoolean","COPY",EDGE,{"derivedFrom":makeQuery(id+"F7.opExtrude","CAP_EDGE",EDGE,{"disambiguationData":[OSD([sQuery(id+"F6.wireOp",EDGE,"E6.62.0")])],"isStart":true})});
            var Q60;
            Q60=makeQuery(id+"F7.boolean.opBoolean","COPY",EDGE,{"derivedFrom":makeQuery(id+"F7.opExtrude","CAP_EDGE",EDGE,{"disambiguationData":[OSD([sQuery(id+"F6.wireOp",EDGE,"E6.63.0")])],"isStart":true})});
            var Q61;
            Q61=makeQuery(id+"F7.boolean.opBoolean","COPY",EDGE,{"derivedFrom":makeQuery(id+"F7.opExtrude","CAP_EDGE",EDGE,{"disambiguationData":[OSD([sQuery(id+"F6.wireOp",EDGE,"E6.64.0")])],"isStart":true})});
            var Q62;
            Q62=makeQuery(id+"F7.boolean.opBoolean","COPY",EDGE,{"derivedFrom":makeQuery(id+"F7.opExtrude","CAP_EDGE",EDGE,{"disambiguationData":[OSD([sQuery(id+"F6.wireOp",EDGE,"E6.66.0")])],"isStart":true})});
            var Q63;
            Q63=makeQuery(id+"F7.boolean.opBoolean","COPY",EDGE,{"derivedFrom":makeQuery(id+"F7.opExtrude","CAP_EDGE",EDGE,{"disambiguationData":[OSD([sQuery(id+"F6.wireOp",EDGE,"E6.65.0")])],"isStart":true})});
            var Q64;
            Q64=makeQuery(id+"F7.boolean.opBoolean","COPY",EDGE,{"derivedFrom":makeQuery(id+"F7.opExtrude","CAP_EDGE",EDGE,{"disambiguationData":[OSD([sQuery(id+"F6.wireOp",EDGE,"E6.67.0")])],"isStart":true})});
            var Q65;
            Q65=makeQuery(id+"F7.boolean.opBoolean","COPY",EDGE,{"derivedFrom":makeQuery(id+"F7.opExtrude","CAP_EDGE",EDGE,{"disambiguationData":[OSD([sQuery(id+"F6.wireOp",EDGE,"E6.68.0")])],"isStart":true})});
            var Q66;
            Q66=makeQuery(id+"F7.boolean.opBoolean","COPY",EDGE,{"derivedFrom":makeQuery(id+"F7.opExtrude","CAP_EDGE",EDGE,{"disambiguationData":[OSD([sQuery(id+"F6.wireOp",EDGE,"E6.69.0")])],"isStart":true})});
            var Q67;
            Q67=makeQuery(id+"F7.boolean.opBoolean","COPY",EDGE,{"derivedFrom":makeQuery(id+"F7.opExtrude","CAP_EDGE",EDGE,{"disambiguationData":[OSD([sQuery(id+"F6.wireOp",EDGE,"E6.70.0")])],"isStart":true})});
            var Q68;
            Q68=makeQuery(id+"F7.boolean.opBoolean","COPY",EDGE,{"derivedFrom":makeQuery(id+"F7.opExtrude","CAP_EDGE",EDGE,{"disambiguationData":[OSD([sQuery(id+"F6.wireOp",EDGE,"E4")])],"isStart":true})});
            var Q69;
            Q69=makeQuery(id+"F7.boolean.opBoolean","COPY",EDGE,{"derivedFrom":makeQuery(id+"F7.opExtrude","CAP_EDGE",EDGE,{"disambiguationData":[OSD([sQuery(id+"F6.wireOp",EDGE,"E5")])],"isStart":true})});
            var Q70;
            Q70=makeQuery(id+"F7.boolean.opBoolean","COPY",EDGE,{"derivedFrom":makeQuery(id+"F7.opExtrude","CAP_EDGE",EDGE,{"disambiguationData":[OSD([sQuery(id+"F6.wireOp",EDGE,"E6.1.0")])],"isStart":true})});
            fillet(context, id + "F8", {"entities" : qUnion([Q0, Q1, Q2, Q3, Q4, Q5, Q6, Q7, Q8, Q9, Q10, Q11, Q12, Q13, Q14, Q15, Q16, Q17, Q18, Q19, Q20, Q21, Q22, Q23, Q24, Q25, Q26, Q27, Q28, Q29, Q30, Q31, Q32, Q33, Q34, Q35, Q36, Q37, Q38, Q39, Q40, Q41, Q42, Q43, Q44, Q45, Q46, Q47, Q48, Q49, Q50, Q51, Q52, Q53, Q54, Q55, Q56, Q57, Q58, Q59, Q60, Q61, Q62, Q63, Q64, Q65, Q66, Q67, Q68, Q69, Q70]), "radius" : 1 * mm, "tangentPropagation" : true, "allowEdgeOverflow" : false});
        }
        {
            var Q0;
            Q0=makeQuery(id+"F3.opExtrude","CAP_FACE",FACE,{"disambiguationData":[OSD([sQuery(id+"F2.wireOp",EDGE,"E1")])],"isStart":false});
            var sketch = newSketch(context, id + "F9", { "sketchPlane" : qUnion([Q0])});
            skCircle(sketch, "E7", {"center": v(0, 0) * mm, "radius": 4.83 * mm});
            skSolve(sketch);
        }
        {
            var Q0;
            Q0=makeQuery(id+"F9.imprint","IMPRINT",FACE,{"disambiguationData":[TD([[makeQuery(id+"F9.imprint","IMPRINT",EDGE,{"derivedFrom":sQuery(id+"F9.wireOp",EDGE,"E7")}),1.0]])]});
            extrude(context, id + "F10", {"entities" : qUnion([Q0]), "operationType" : NewBodyOperationType.REMOVE, "endBound" : BoundingType.UP_TO_NEXT, "oppositeDirection" : true, "depth" : 25 * mm, "offsetDistance" : 25 * mm});
        }
    });
